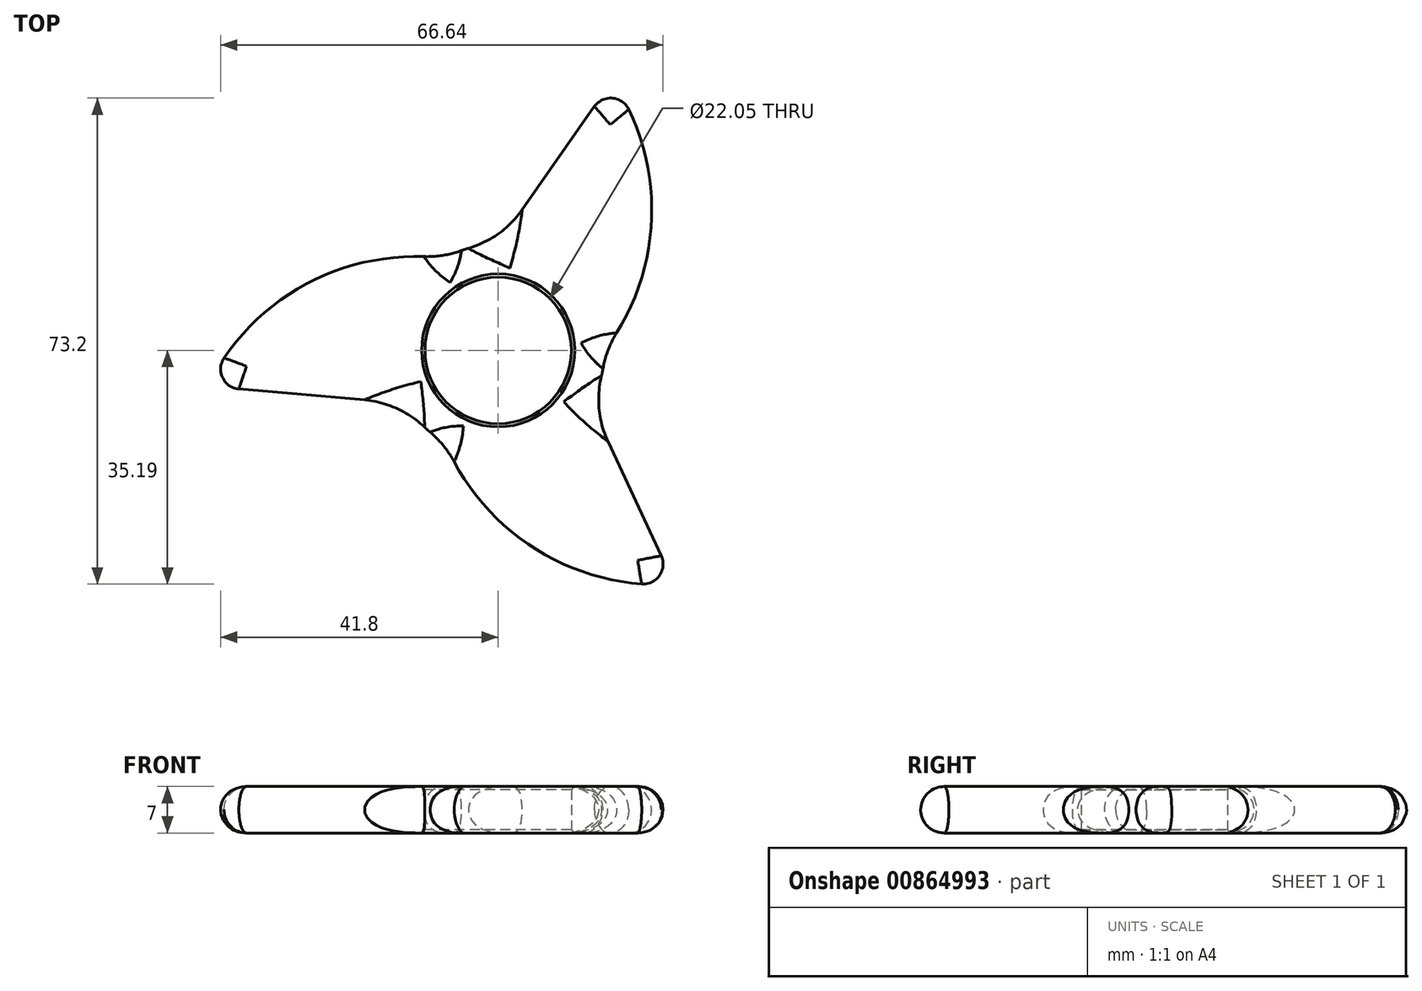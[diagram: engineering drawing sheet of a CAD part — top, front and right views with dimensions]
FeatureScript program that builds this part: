
annotation { "Feature Type Name" : "Feature", "Feature Type Description" : "" }
export const myFeature = defineFeature(function(context is Context, id is Id, definition is map)
    precondition{}
    {
        {
            var Q0;
            Q0=qCreatedBy(makeId("Top.planeOp"),FACE);
            var sketch = newSketch(context, id + "F0", { "sketchPlane" : qUnion([Q0])});
            skCircle(sketch, "E0", {"center": v(0, 0) * mm, "radius": 11.03 * mm});
            skCircle(sketch, "E1", {"center": v(0, 0) * mm, "radius": 16.03 * mm});
            skLineSegment(sketch, "E2", {"start": v(0, 16.02) * mm, "end": v(14.5, 36.73) * mm});
            skArc(sketch, "E3", {"start": v(16.03, 0) * mm, "mid": v(22.95, 17.64) * mm, "end": v(19.66, 36.31) * mm});
            skPoint(sketch, "E4.visualSharp", {"position": v(17.2, 40.6) * mm});
            skArc(sketch, "E4.filletArc", {"start": v(19.66, 36.31) * mm, "mid": v(17.2, 38) * mm, "end": v(14.5, 36.73) * mm});
            skSolve(sketch);
        }
        {
            var Q0;
            Q0=qSketchRegion(id+"F0",true);
            extrude(context, id + "F1", {"entities" : qUnion([Q0]), "depth" : 7 * mm, "offsetDistance" : 25 * mm});
        }
        {
            var Q0;
            Q0=qCreatedBy(makeId("Right.planeOp"),FACE);
            var sketch = newSketch(context, id + "F2", { "sketchPlane" : qUnion([Q0])});
            skLineSegment(sketch, "E5", {"start": v(0, 0) * mm, "end": v(0, -17.5) * mm});
            skSolve(sketch);
        }
        {
            var Q0;
            Q0=makeQuery(id+"F1.opExtrude","CAP_EDGE",EDGE,{"disambiguationData":[OSD([sQuery(id+"F0.wireOp",EDGE,"E3")])],"isStart":false});
            var Q1;
            Q1=makeQuery(id+"F1.opExtrude","CAP_EDGE",EDGE,{"disambiguationData":[OSD([sQuery(id+"F0.wireOp",EDGE,"E3")])],"isStart":true});
            var Q2;
            Q2=makeQuery(id+"F1.opExtrude","CAP_EDGE",EDGE,{"disambiguationData":[OSD([sQuery(id+"F0.wireOp",EDGE,"E1")])],"isStart":true});
            var Q3;
            Q3=makeQuery(id+"F1.opExtrude","CAP_EDGE",EDGE,{"disambiguationData":[OSD([sQuery(id+"F0.wireOp",EDGE,"E1")])],"isStart":false});
            fillet(context, id + "F3", {"entities" : qUnion([Q0, Q1, Q2, Q3]), "radius" : 3.5 * mm, "tangentPropagation" : true, "allowEdgeOverflow" : false});
        }
        {
            var Q0;
            Q0=makeQuery(id+"F1.opExtrude","SWEPT_BODY",BODY,{"disambiguationData":[OSD([sQuery(id+"F0.wireOp",EDGE,"E0"),sQuery(id+"F0.wireOp",EDGE,"E1"),sQuery(id+"F0.wireOp",EDGE,"E2"),sQuery(id+"F0.wireOp",EDGE,"E3"),sQuery(id+"F0.wireOp",EDGE,"E4.filletArc")])]});
            var Q1;
            Q1=sQuery(id+"F2.wireOp",EDGE,"E5");
            circularPattern(context, id + "F4", {"entities" : qUnion([Q0]), "axis" : qUnion([Q1]), "angle" : 360 * degree, "instanceCount" : 3, "equalSpace" : true});
        }
        {
            var Q0;
            Q0=makeQuery(id+"F1.opExtrude","SWEPT_BODY",BODY,{"disambiguationData":[OSD([sQuery(id+"F0.wireOp",EDGE,"E0"),sQuery(id+"F0.wireOp",EDGE,"E1"),sQuery(id+"F0.wireOp",EDGE,"E2"),sQuery(id+"F0.wireOp",EDGE,"E3"),sQuery(id+"F0.wireOp",EDGE,"E4.filletArc")])]});
            var Q1;
            Q1=makeQuery(id+"F4.opPattern","COPY",BODY,{"derivedFrom":makeQuery(id+"F1.opExtrude","SWEPT_BODY",BODY,{"disambiguationData":[OSD([sQuery(id+"F0.wireOp",EDGE,"E0"),sQuery(id+"F0.wireOp",EDGE,"E1"),sQuery(id+"F0.wireOp",EDGE,"E2"),sQuery(id+"F0.wireOp",EDGE,"E3"),sQuery(id+"F0.wireOp",EDGE,"E4.filletArc")])]}),"instanceName":"1"});
            var Q2;
            Q2=makeQuery(id+"F4.opPattern","COPY",BODY,{"derivedFrom":makeQuery(id+"F1.opExtrude","SWEPT_BODY",BODY,{"disambiguationData":[OSD([sQuery(id+"F0.wireOp",EDGE,"E0"),sQuery(id+"F0.wireOp",EDGE,"E1"),sQuery(id+"F0.wireOp",EDGE,"E2"),sQuery(id+"F0.wireOp",EDGE,"E3"),sQuery(id+"F0.wireOp",EDGE,"E4.filletArc")])]}),"instanceName":"2"});
            booleanBodies(context, id + "F5", {"operationType" : BooleanOperationType.UNION, "tools" : qUnion([Q0, Q1, Q2])});
        }
        {
            var Q0;
            {var subQ0=sQuery(id+"F0.wireOp",EDGE,"E2");var subQ1=sQuery(id+"F0.wireOp",EDGE,"E1");Q0=makeQuery(id+"F5.opBoolean","MERGE",EDGE,{"derivedFrom":[makeQuery(id+"F3.opFillet","BLEND_EDGE",EDGE,{"blendedFrom":[makeQuery(id+"F1.opExtrude","CAP_EDGE",EDGE,{"disambiguationData":[OSD([subQ1])],"isStart":true}),makeQuery(id+"F1.opExtrude","CAP_EDGE",EDGE,{"disambiguationData":[OSD([subQ0])],"isStart":true})],"blendedInto":[]}),makeQuery(id+"F3.opFillet","BLEND_EDGE",EDGE,{"blendedFrom":[makeQuery(id+"F1.opExtrude","CAP_EDGE",EDGE,{"disambiguationData":[OSD([subQ1])],"isStart":false}),makeQuery(id+"F1.opExtrude","CAP_EDGE",EDGE,{"disambiguationData":[OSD([subQ0])],"isStart":false})],"blendedInto":[]})]});}
            var Q1;
            {var subQ0=sQuery(id+"F0.wireOp",EDGE,"E3");var subQ1=sQuery(id+"F0.wireOp",EDGE,"E1");Q1=makeQuery(id+"F5.opBoolean","MERGE",EDGE,{"derivedFrom":[makeQuery(id+"F4.opPattern","COPY",EDGE,{"derivedFrom":makeQuery(id+"F3.opFillet","BLEND_EDGE",EDGE,{"blendedFrom":[makeQuery(id+"F1.opExtrude","CAP_EDGE",EDGE,{"disambiguationData":[OSD([subQ1])],"isStart":true}),makeQuery(id+"F1.opExtrude","CAP_EDGE",EDGE,{"disambiguationData":[OSD([subQ0])],"isStart":true})],"blendedInto":[]}),"instanceName":"2"}),makeQuery(id+"F4.opPattern","COPY",EDGE,{"derivedFrom":makeQuery(id+"F3.opFillet","BLEND_EDGE",EDGE,{"blendedFrom":[makeQuery(id+"F1.opExtrude","CAP_EDGE",EDGE,{"disambiguationData":[OSD([subQ1])],"isStart":false}),makeQuery(id+"F1.opExtrude","CAP_EDGE",EDGE,{"disambiguationData":[OSD([subQ0])],"isStart":false})],"blendedInto":[]}),"instanceName":"2"})]});}
            var Q2;
            {var subQ0=sQuery(id+"F0.wireOp",EDGE,"E3");var subQ1=sQuery(id+"F0.wireOp",EDGE,"E1");Q2=makeQuery(id+"F5.opBoolean","MERGE",EDGE,{"derivedFrom":[makeQuery(id+"F3.opFillet","BLEND_EDGE",EDGE,{"blendedFrom":[makeQuery(id+"F1.opExtrude","CAP_EDGE",EDGE,{"disambiguationData":[OSD([subQ1])],"isStart":true}),makeQuery(id+"F1.opExtrude","CAP_EDGE",EDGE,{"disambiguationData":[OSD([subQ0])],"isStart":true})],"blendedInto":[]}),makeQuery(id+"F3.opFillet","BLEND_EDGE",EDGE,{"blendedFrom":[makeQuery(id+"F1.opExtrude","CAP_EDGE",EDGE,{"disambiguationData":[OSD([subQ1])],"isStart":false}),makeQuery(id+"F1.opExtrude","CAP_EDGE",EDGE,{"disambiguationData":[OSD([subQ0])],"isStart":false})],"blendedInto":[]})]});}
            var Q3;
            {var subQ0=sQuery(id+"F0.wireOp",EDGE,"E2");var subQ1=sQuery(id+"F0.wireOp",EDGE,"E1");Q3=makeQuery(id+"F5.opBoolean","MERGE",EDGE,{"derivedFrom":[makeQuery(id+"F4.opPattern","COPY",EDGE,{"derivedFrom":makeQuery(id+"F3.opFillet","BLEND_EDGE",EDGE,{"blendedFrom":[makeQuery(id+"F1.opExtrude","CAP_EDGE",EDGE,{"disambiguationData":[OSD([subQ1])],"isStart":true}),makeQuery(id+"F1.opExtrude","CAP_EDGE",EDGE,{"disambiguationData":[OSD([subQ0])],"isStart":true})],"blendedInto":[]}),"instanceName":"1"}),makeQuery(id+"F4.opPattern","COPY",EDGE,{"derivedFrom":makeQuery(id+"F3.opFillet","BLEND_EDGE",EDGE,{"blendedFrom":[makeQuery(id+"F1.opExtrude","CAP_EDGE",EDGE,{"disambiguationData":[OSD([subQ1])],"isStart":false}),makeQuery(id+"F1.opExtrude","CAP_EDGE",EDGE,{"disambiguationData":[OSD([subQ0])],"isStart":false})],"blendedInto":[]}),"instanceName":"1"})]});}
            var Q4;
            {var subQ0=sQuery(id+"F0.wireOp",EDGE,"E3");var subQ1=sQuery(id+"F0.wireOp",EDGE,"E1");Q4=makeQuery(id+"F5.opBoolean","MERGE",EDGE,{"derivedFrom":[makeQuery(id+"F4.opPattern","COPY",EDGE,{"derivedFrom":makeQuery(id+"F3.opFillet","BLEND_EDGE",EDGE,{"blendedFrom":[makeQuery(id+"F1.opExtrude","CAP_EDGE",EDGE,{"disambiguationData":[OSD([subQ1])],"isStart":true}),makeQuery(id+"F1.opExtrude","CAP_EDGE",EDGE,{"disambiguationData":[OSD([subQ0])],"isStart":true})],"blendedInto":[]}),"instanceName":"1"}),makeQuery(id+"F4.opPattern","COPY",EDGE,{"derivedFrom":makeQuery(id+"F3.opFillet","BLEND_EDGE",EDGE,{"blendedFrom":[makeQuery(id+"F1.opExtrude","CAP_EDGE",EDGE,{"disambiguationData":[OSD([subQ1])],"isStart":false}),makeQuery(id+"F1.opExtrude","CAP_EDGE",EDGE,{"disambiguationData":[OSD([subQ0])],"isStart":false})],"blendedInto":[]}),"instanceName":"1"})]});}
            var Q5;
            {var subQ0=sQuery(id+"F0.wireOp",EDGE,"E2");var subQ1=sQuery(id+"F0.wireOp",EDGE,"E1");Q5=makeQuery(id+"F5.opBoolean","MERGE",EDGE,{"derivedFrom":[makeQuery(id+"F4.opPattern","COPY",EDGE,{"derivedFrom":makeQuery(id+"F3.opFillet","BLEND_EDGE",EDGE,{"blendedFrom":[makeQuery(id+"F1.opExtrude","CAP_EDGE",EDGE,{"disambiguationData":[OSD([subQ1])],"isStart":true}),makeQuery(id+"F1.opExtrude","CAP_EDGE",EDGE,{"disambiguationData":[OSD([subQ0])],"isStart":true})],"blendedInto":[]}),"instanceName":"2"}),makeQuery(id+"F4.opPattern","COPY",EDGE,{"derivedFrom":makeQuery(id+"F3.opFillet","BLEND_EDGE",EDGE,{"blendedFrom":[makeQuery(id+"F1.opExtrude","CAP_EDGE",EDGE,{"disambiguationData":[OSD([subQ1])],"isStart":false}),makeQuery(id+"F1.opExtrude","CAP_EDGE",EDGE,{"disambiguationData":[OSD([subQ0])],"isStart":false})],"blendedInto":[]}),"instanceName":"2"})]});}
            fillet(context, id + "F6", {"entities" : qUnion([Q0, Q1, Q2, Q3, Q4, Q5]), "radius" : 15 * mm, "tangentPropagation" : true, "allowEdgeOverflow" : false});
        }
        {
            var Q0;
            Q0=makeQuery(id+"F1.opExtrude","CAP_EDGE",EDGE,{"disambiguationData":[OSD([sQuery(id+"F0.wireOp",EDGE,"E0")])],"isStart":false});
            var Q1;
            Q1=makeQuery(id+"F1.opExtrude","CAP_EDGE",EDGE,{"disambiguationData":[OSD([sQuery(id+"F0.wireOp",EDGE,"E0")])],"isStart":true});
            chamfer(context, id + "F7", {"entities" : qUnion([Q0, Q1]), "width" : .5 * mm, "tangentPropagation" : true});
        }
    });
